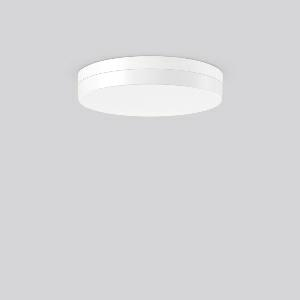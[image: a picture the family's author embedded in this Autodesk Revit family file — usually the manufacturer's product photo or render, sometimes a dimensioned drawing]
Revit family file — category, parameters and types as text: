
# Revit family: flat_slim_round_312632_002_1_19_d614
name_source: partatom
category: Lighting Fixtures
units: mm (PartAtom-declared; Revit-internal decimal feet)

## family parameters
Cut with Voids When Loaded = No
Host = Face
Light Source = No
Part Type = Normal
Room Calculation Point = No
Round Connector Dimension = Use Diameter
Shared = No

## types (1)
- MultiLumen 1 830 (1 x LED Modul 830, 2450 lm, 3000)
    Apparent Load = 18 VA
    CIE Flux Codes = 37 67 88 84 100
    Color Rendering = 80
    Color Temperature = 3000
    Default Elevation = 1800 mm
    Height = 70 mm
    Lamp = 1 x LED Modul 830
    Lamp Light Flux = 2450 lm
    Lamp count = 1
    Length = 400 mm
    Lifetime = 50000 h
    Luminous efficacy = 136 lm/W
    Manufacturer = RZB
    ModVariant = No
    Model = 312632.002.1.19
    Mounting Place = Ceiling
    Mounting Type = Surface mounted
    Number of Poles = 1
    OnlyDefault = Yes
    Power Factor = 1
    Product Name = FLAT SLIM round
    Product group = Surface mounted ceiling and wall luminaires
    ProductGroupID = 305
    Protection Class = Protection class I
    Protection Degree = Degree of protection
    RLX_Detail_Level = 1
    RLX_Emergency_Light_Flux = 0 lm
    RLX_Emergency_Type = 0
    RLX_Emergency_Type_DB = No
    RlxData = <blob elided: 20577 chars, md5=c059247a>
    Socket = socket
    Standby Power = 0 W
    System Light Flux = 2450 lm
    System Power = 18 W
    Type Comments = MultiLumen 1 830
    Type Image = 312631.002.jpg
    URL = http://relux.com
    VarID = multilumen_1_830
    Voltage = 0 V
    Weight = 0.00 kg
    Width = 0 mm  [stored 0 ft]

note: [stored X ft] marks values corroborated as IEEE doubles in the binary element streams (Revit-internal decimal feet)

## geometry (parser evidence)
native form markers: Blend x4, Sweep x12
no freeform markers — native parametric forms only
